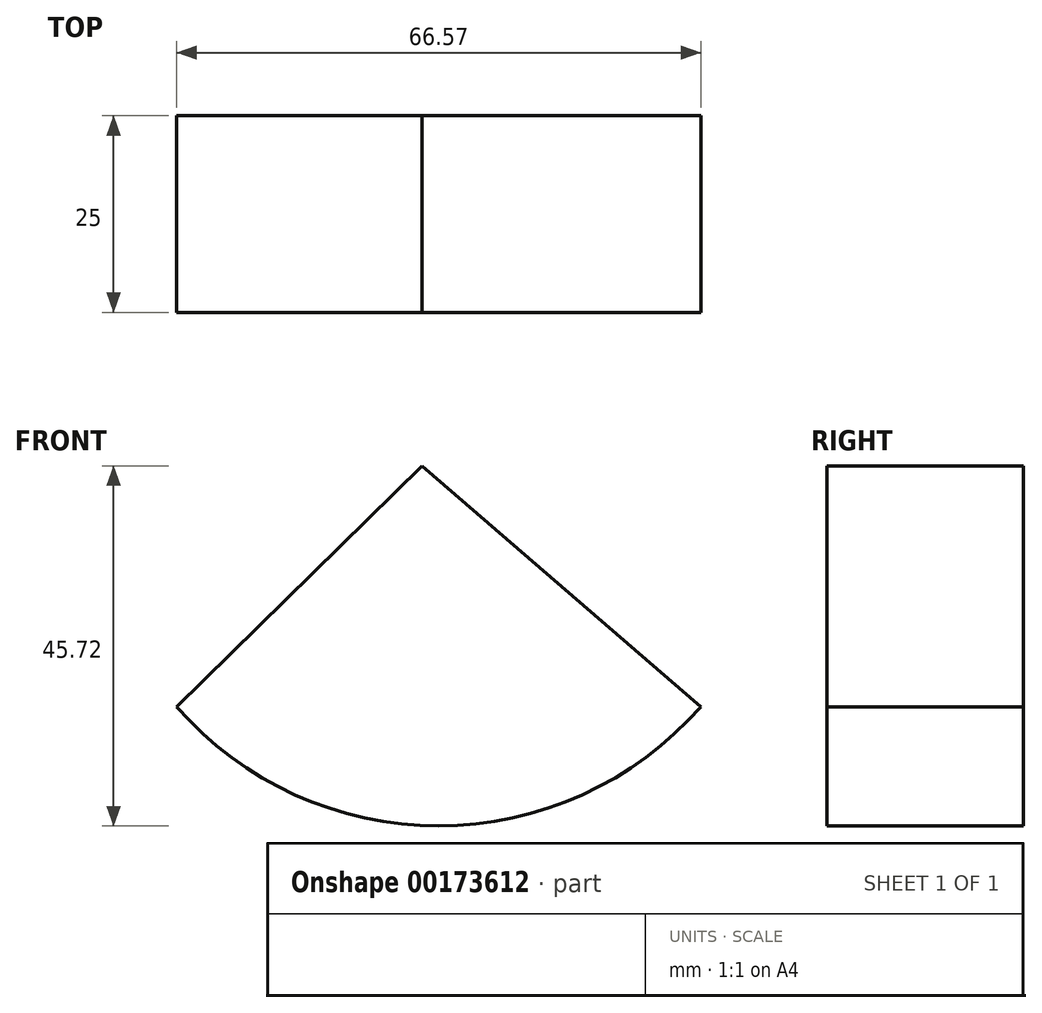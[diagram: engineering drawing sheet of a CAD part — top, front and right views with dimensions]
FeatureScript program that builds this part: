
annotation { "Feature Type Name" : "Feature", "Feature Type Description" : "" }
export const myFeature = defineFeature(function(context is Context, id is Id, definition is map)
    precondition{}
    {
        {
            var Q0;
            Q0=qCreatedBy(makeId("Front.planeOp"),FACE);
            var sketch = newSketch(context, id + "F0", { "sketchPlane" : qUnion([Q0])});
            skLineSegment(sketch, "E0", {"start": v(0, 30.6) * mm, "end": v(-31.16, 0) * mm});
            skLineSegment(sketch, "E1", {"start": v(0, 30.6) * mm, "end": v(35.4, 0) * mm});
            skArc(sketch, "E2", {"start": v(-31.16, 0) * mm, "mid": v(2.12, -15.13) * mm, "end": v(35.4, 0) * mm});
            skSolve(sketch);
        }
        {
            var Q0;
            Q0 = qSketchRegion(id + "F0", true);
            extrude(context, id + "F1", {"entities" : qUnion([Q0]), "endBound" : BoundingType.SYMMETRIC, "oppositeDirection" : true, "depth" : 25 * mm});
        }
    });
